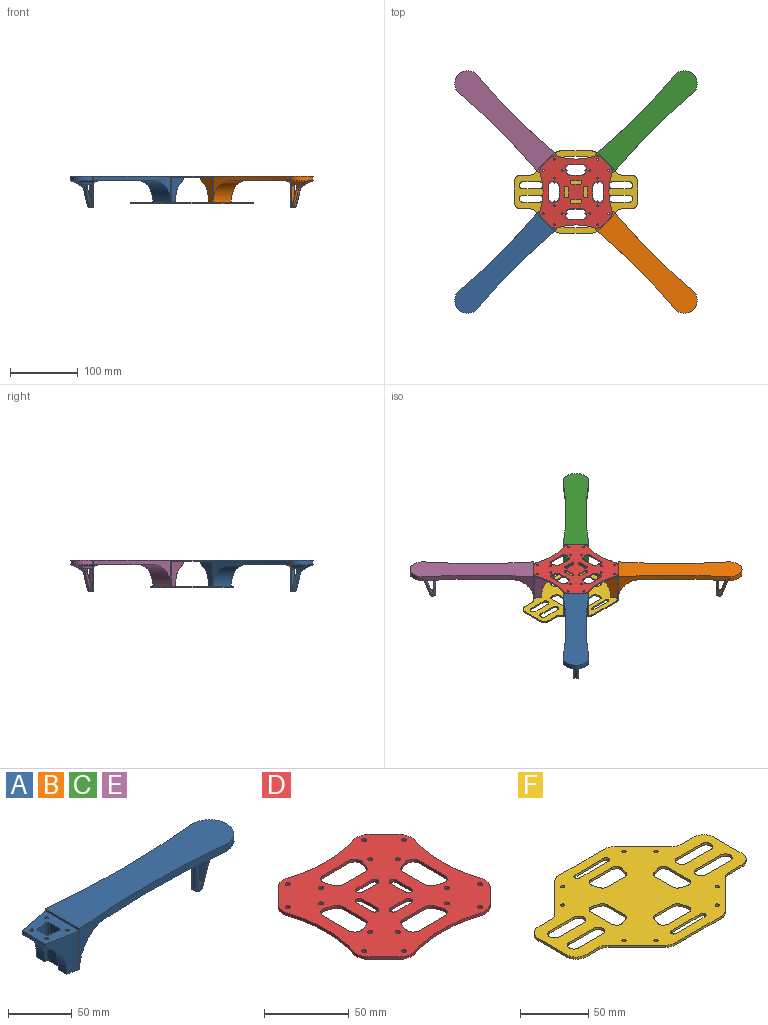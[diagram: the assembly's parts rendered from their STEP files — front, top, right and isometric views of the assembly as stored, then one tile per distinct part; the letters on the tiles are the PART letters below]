
ASSEMBLY  parts=6 mates=5
PART A: 66 faces, bbox 214.6x38.9x48 mm
  f0: plane 0.16x0.01mm, normal (0,-1,0), area 0mm2, adj f5,f44,f63
  f1: plane 0.16x0.01mm, normal (0,1,0), area 0mm2, adj f3,f46,f63
  f2: plane 19.09x12.46mm, normal (0.45,0,-0.89), area 107.7mm2, adj f4,f6,f34,f43,f52,f57
  f3: cylinder r=5mm len=41.67mm, axis (-1,0,0), area 242.4mm2, adj f1,f4,f7,f34,f39,f47,f60
  f4: bspline ~14.02x6.57mm, area 32.6mm2, adj f2,f3,f34,f52
  f5: cylinder r=5mm len=41.67mm, axis (1,0,0), area 242.4mm2, adj f0,f6,f7,f34,f38,f45,f60
  f6: bspline ~17.01x8.06mm, area 32.6mm2, adj f2,f5,f34,f57
  f7: plane 147.98x38.01mm, normal (0,0,-1), area 4011.6mm2, adj f3,f5,f9,f10,f11,f32,f33,f34
  f8: plane 181.92x38.01mm, normal (0,0,1), area 5871.4mm2, adj f10,f11,f31,f32,f33,f34,f35,f36
  f9: cylinder r=31.8mm len=37.96mm, axis (0,1,0), area 1777.7mm2, adj f7,f13,f32,f33,f35,f36
  f10: plane 7x0.96mm, normal (0,-1,0), area 6.7mm2, adj f7,f8,f33,f34
  f11: plane 7x0.96mm, normal (0,1,0), area 6.7mm2, adj f7,f8,f32,f34
  f12: extruded ~33.43x30.75mm, area 739mm2, adj f13,f15,f17,f18,f19,f22,f23,f24
  f13: plane 37.92x12mm, normal (0,0,-1), area 370mm2, adj f9,f12,f15,f17,f20,f21,f23,f27
  f14: plane 37.92x31.65mm, normal (0,0,1), area 800.9mm2, adj f15,f16,f17,f19,f20,f21,f22,f23
  f15: plane 37.07x30.99mm, normal (-0.19,0.98,0), area 651.5mm2, adj f12,f13,f14,f16,f18,f36
  f16: plane 25.93x1.4mm, normal (-1,0,0), area 36.3mm2, adj f14,f15,f17,f18
  f17: plane 37.07x30.99mm, normal (-0.19,-0.98,0), area 651.5mm2, adj f12,f13,f14,f16,f18,f35
  f18: cylinder r=5mm len=27.13mm, axis (0,1,0), area 158.4mm2, adj f12,f15,f16,f17
  f19: cylinder r=1.5mm len=8.24mm, axis (0,0,1), area 69.7mm2, adj f12,f14
  f20: cylinder r=1.5mm len=36.8mm, axis (0,0,1), area 346.8mm2, adj f13,f14
  f21: cylinder r=1.5mm len=36.8mm, axis (0,0,1), area 346.8mm2, adj f13,f14
  f22: cylinder r=1.5mm len=8.24mm, axis (0,0,1), area 69.7mm2, adj f12,f14
  f23: plane 36.8x9.65mm, normal (0.19,-0.98,0), area 183.9mm2, adj f12,f13,f14,f24,f29
  f24: cylinder r=2mm len=10.6mm, axis (0,0,1), area 27.5mm2, adj f12,f14,f23,f25
  f25: plane 9.27x7.73mm, normal (1,0,0), area 71.6mm2, adj f12,f14,f24,f26
  f26: cylinder r=2mm len=10.6mm, axis (0,0,1), area 27.5mm2, adj f12,f14,f25,f27
  f27: plane 36.8x9.65mm, normal (0.19,0.98,0), area 183.9mm2, adj f12,f13,f14,f26,f30
  f28: plane 36.8x11.41mm, normal (-1,0,0), area 419.9mm2, adj f13,f14,f29,f30
  f29: cylinder r=2mm len=36.8mm, axis (0,0,1), area 129.5mm2, adj f13,f14,f23,f28
  f30: cylinder r=2mm len=36.8mm, axis (0,0,1), area 129.5mm2, adj f13,f14,f27,f28
  f31: plane 37.92x2mm, normal (-1,0,0), area 75.8mm2, adj f8,f14,f35,f36
  f32: cylinder r=800mm len=161.71mm, axis (0,0,-1), area 1344.7mm2, adj f7,f8,f9,f11,f36
  f33: cylinder r=800mm len=161.71mm, axis (0,0,-1), area 1344.7mm2, adj f7,f8,f9,f10,f35
  f34: cylinder r=19mm len=38.01mm, axis (0,0,-1), area 424.8mm2, adj f2,f3,f4,f5,f6,f7,f8,f10
  f35: cylinder r=10mm len=38.8mm, axis (0,0,1), area 43.5mm2, adj f8,f9,f13,f14,f17,f31,f33
  f36: cylinder r=10mm len=38.8mm, axis (0,0,-1), area 43.5mm2, adj f8,f9,f13,f14,f15,f31,f32
  f37: plane 24.74x8.67mm, normal (0.94,0,-0.33), area 91.7mm2, adj f41,f43,f50,f55
  f38: plane 32.81x18.54mm, normal (0,-1,0), area 52.4mm2, adj f5,f44,f54,f55,f56,f57,f58,f59
  f39: plane 32.81x18.54mm, normal (0,1,0), area 52.4mm2, adj f3,f46,f49,f50,f51,f52,f58,f59
  f40: cylinder r=5mm len=17.5mm, axis (0,1,0), area 46.6mm2, adj f7,f45,f47
  f41: cylinder r=5mm len=4.2mm, axis (0,1,0), area 19.6mm2, adj f37,f42,f48,f49,f53,f54
  f42: cylinder r=5mm len=4.32mm, axis (0,1,0), area 15.8mm2, adj f41,f44,f46,f48,f53
  f43: cylinder r=5mm len=3.5mm, axis (0,-1,0), area 13.5mm2, adj f2,f37,f51,f56
  f44: cylinder r=5mm len=33mm, axis (0,0,1), area 164.3mm2, adj f0,f38,f42,f45,f46,f53,f63,f64
  f45: bspline ~10x10mm, area 45.7mm2, adj f5,f40,f44,f47
  f46: cylinder r=5mm len=33mm, axis (0,0,-1), area 164.3mm2, adj f1,f39,f42,f44,f47,f48,f63,f64
  f47: bspline ~10x10mm, area 45.7mm2, adj f3,f40,f45,f46
  f48: bspline ~5.97x3.67mm, area 10.7mm2, adj f41,f42,f46,f49
  f49: torus R=3mm, axis (0,-1,0), area 11.8mm2, adj f39,f41,f48,f50
  f50: cylinder r=2mm len=25.4mm, axis (0.33,0,0.94), area 82.4mm2, adj f37,f39,f49,f51
  f51: torus R=7mm, axis (0,-1,0), area 13.9mm2, adj f39,f43,f50,f52
  f52: cylinder r=2mm len=5.5mm, axis (0.89,0,0.45), area 16.2mm2, adj f2,f4,f39,f51
  f53: bspline ~5.97x3.67mm, area 10.7mm2, adj f41,f42,f44,f54
  f54: torus R=3mm, axis (0,-1,0), area 11.8mm2, adj f38,f41,f53,f55
  f55: cylinder r=2mm len=25.4mm, axis (-0.33,0,-0.94), area 82.4mm2, adj f37,f38,f54,f56
  f56: torus R=7mm, axis (0,-1,0), area 13.9mm2, adj f38,f43,f55,f57
  f57: cylinder r=2mm len=5.5mm, axis (-0.89,0,-0.45), area 16.2mm2, adj f2,f6,f38,f56
  f58: plane 23.99x8.4mm, normal (-0.94,0,0.33), area 190.7mm2, adj f38,f39,f59,f62
  f59: cylinder r=2mm len=7.5mm, axis (0,-1,0), area 28.6mm2, adj f38,f39,f58,f60
  f60: plane 8.6x7.5mm, normal (0,0,-1), area 64.5mm2, adj f3,f5,f59,f63
  f61: plane 7.5x0.2mm, normal (0,0,1), area 1.5mm2, adj f38,f39,f62,f64
  f62: cylinder r=2mm len=7.5mm, axis (0,-1,0), area 18.5mm2, adj f38,f39,f58,f61
  f63: cylinder r=2mm len=7.5mm, axis (0,-1,0), area 22.5mm2, adj f0,f1,f44,f46,f60,f65
  f64: cylinder r=2mm len=7.5mm, axis (0,-1,0), area 22.5mm2, adj f38,f39,f44,f46,f61,f65
  f65: plane 23.99x6.8mm, normal (1,0,0), area 163.1mm2, adj f44,f46,f63,f64
PART B: same geometry as A
PART C: same geometry as A
PART D: 82 faces, bbox 106.8x106.8x2 mm
  f0: plane 106.75x106.75mm, normal (0,0,1), area 7803.2mm2, adj f2,f3,f4,f5,f6,f7,f8,f9
  f1: plane 106.75x106.75mm, normal (0,0,-1), area 7803.2mm2, adj f2,f3,f4,f5,f6,f7,f8,f9
  f2: plane 12.51x12.51mm, normal (0.71,0.71,0), area 35.4mm2, adj f0,f1,f10,f12
  f3: plane 12.51x12.51mm, normal (-0.71,0.71,0), area 35.4mm2, adj f0,f1,f13,f16
  f4: plane 12.51x12.51mm, normal (-0.71,-0.71,0), area 35.4mm2, adj f0,f1,f14,f17
  f5: plane 12.51x12.51mm, normal (0.71,-0.71,0), area 35.4mm2, adj f0,f1,f11,f15
  f6: cylinder r=90mm len=55.57mm, axis (0,0,-1), area 113mm2, adj f0,f1,f16,f17
  f7: cylinder r=90mm len=55.57mm, axis (0,0,-1), area 113mm2, adj f0,f1,f14,f15
  f8: cylinder r=90mm len=55.57mm, axis (0,0,-1), area 113mm2, adj f0,f1,f12,f13
  f9: cylinder r=90mm len=55.57mm, axis (0,0,-1), area 113mm2, adj f0,f1,f10,f11
  f10: cylinder r=10mm len=10.16mm, axis (0,0,-1), area 22mm2, adj f0,f1,f2,f9
  f11: cylinder r=10mm len=10.16mm, axis (0,0,-1), area 22mm2, adj f0,f1,f5,f9
  f12: cylinder r=10mm len=10.16mm, axis (0,0,-1), area 22mm2, adj f0,f1,f2,f8
  f13: cylinder r=10mm len=10.16mm, axis (0,0,-1), area 22mm2, adj f0,f1,f3,f8
  f14: cylinder r=10mm len=10.16mm, axis (0,0,-1), area 22mm2, adj f0,f1,f4,f7
  f15: cylinder r=10mm len=10.16mm, axis (0,0,-1), area 22mm2, adj f0,f1,f5,f7
  f16: cylinder r=10mm len=10.16mm, axis (0,0,-1), area 22mm2, adj f0,f1,f3,f6
  f17: cylinder r=10mm len=10.16mm, axis (0,0,-1), area 22mm2, adj f0,f1,f4,f6
  f18: cylinder r=1.5mm len=3mm, axis (0,0,1), area 18.8mm2, adj f0,f1
  f19: cylinder r=1.5mm len=3mm, axis (0,0,1), area 18.8mm2, adj f0,f1
  f20: cylinder r=1.5mm len=3mm, axis (0,0,1), area 18.8mm2, adj f0,f1
  f21: cylinder r=1.5mm len=3mm, axis (0,0,1), area 18.8mm2, adj f0,f1
  f22: cylinder r=1.5mm len=3mm, axis (0,0,1), area 18.8mm2, adj f0,f1
  f23: cylinder r=1.5mm len=3mm, axis (0,0,1), area 18.8mm2, adj f0,f1
  f24: cylinder r=1.5mm len=3mm, axis (0,0,1), area 18.8mm2, adj f0,f1
  f25: cylinder r=1.5mm len=3mm, axis (0,0,1), area 18.8mm2, adj f0,f1
  f26: cylinder r=1.5mm len=3mm, axis (0,0,1), area 18.8mm2, adj f0,f1
  f27: cylinder r=1.5mm len=3mm, axis (0,0,1), area 18.8mm2, adj f0,f1
  f28: cylinder r=1.5mm len=3mm, axis (0,0,1), area 18.8mm2, adj f0,f1
  f29: cylinder r=1.5mm len=3mm, axis (0,0,1), area 18.8mm2, adj f0,f1
  f30: cylinder r=1.5mm len=3mm, axis (0,0,1), area 18.8mm2, adj f0,f1
  f31: cylinder r=1.5mm len=3mm, axis (0,0,1), area 18.8mm2, adj f0,f1
  f32: cylinder r=1.5mm len=3mm, axis (0,0,1), area 18.8mm2, adj f0,f1
  f33: cylinder r=1.5mm len=3mm, axis (0,0,1), area 18.8mm2, adj f0,f1
  f34: plane 12.5x2mm, normal (0,-1,0), area 25mm2, adj f0,f1,f35,f37
  f35: cylinder r=2.5mm len=5mm, axis (0,0,1), area 15.7mm2, adj f0,f1,f34,f36
  f36: plane 12.5x2mm, normal (0,1,0), area 25mm2, adj f0,f1,f35,f37
  f37: cylinder r=2.5mm len=5mm, axis (0,0,1), area 15.7mm2, adj f0,f1,f34,f36
  f38: plane 5x2mm, normal (0.32,0.95,0), area 10.5mm2, adj f0,f1,f39,f45
  f39: cylinder r=5mm len=6.58mm, axis (0,0,1), area 18.9mm2, adj f0,f1,f38,f40
  f40: plane 21.13x2mm, normal (-1,0,0), area 42.3mm2, adj f0,f1,f39,f41
  f41: cylinder r=5mm len=6.58mm, axis (0,0,1), area 18.9mm2, adj f0,f1,f40,f42
  f42: plane 5x2mm, normal (0.32,-0.95,0), area 10.5mm2, adj f0,f1,f41,f43
  f43: cylinder r=5mm len=4.74mm, axis (0,0,1), area 12.5mm2, adj f0,f1,f42,f44
  f44: plane 17.79x2mm, normal (1,0,0), area 35.6mm2, adj f0,f1,f43,f45
  f45: cylinder r=5mm len=4.74mm, axis (0,0,1), area 12.5mm2, adj f0,f1,f38,f44
  f46: cylinder r=5mm len=6.58mm, axis (0,0,1), area 18.9mm2, adj f0,f1,f47,f53
  f47: plane 21.13x2mm, normal (1,0,0), area 42.3mm2, adj f0,f1,f46,f48
  f48: cylinder r=5mm len=6.58mm, axis (0,0,1), area 18.9mm2, adj f0,f1,f47,f49
  f49: plane 5x2mm, normal (-0.32,0.95,0), area 10.5mm2, adj f0,f1,f48,f50
  f50: cylinder r=5mm len=4.74mm, axis (0,0,1), area 12.5mm2, adj f0,f1,f49,f51
  f51: plane 17.79x2mm, normal (-1,0,0), area 35.6mm2, adj f0,f1,f50,f52
  f52: cylinder r=5mm len=4.74mm, axis (0,0,1), area 12.5mm2, adj f0,f1,f51,f53
  f53: plane 5x2mm, normal (-0.32,-0.95,0), area 10.5mm2, adj f0,f1,f46,f52
  f54: plane 17.79x2mm, normal (0,-1,0), area 35.6mm2, adj f0,f1,f55,f61
  f55: cylinder r=5mm len=4.74mm, axis (0,0,1), area 12.5mm2, adj f0,f1,f54,f56
  f56: plane 5x2mm, normal (0.95,-0.32,0), area 10.5mm2, adj f0,f1,f55,f57
  f57: cylinder r=5mm len=6.58mm, axis (0,0,1), area 18.9mm2, adj f0,f1,f56,f58
  f58: plane 21.13x2mm, normal (0,1,0), area 42.3mm2, adj f0,f1,f57,f59
  f59: cylinder r=5mm len=6.58mm, axis (0,0,1), area 18.9mm2, adj f0,f1,f58,f60
  f60: plane 5x2mm, normal (-0.95,-0.32,0), area 10.5mm2, adj f0,f1,f59,f61
  f61: cylinder r=5mm len=4.74mm, axis (0,0,1), area 12.5mm2, adj f0,f1,f54,f60
  f62: cylinder r=2.5mm len=5mm, axis (0,0,1), area 15.7mm2, adj f0,f1,f63,f65
  f63: plane 12.5x2mm, normal (0,1,0), area 25mm2, adj f0,f1,f62,f64
  f64: cylinder r=2.5mm len=5mm, axis (0,0,1), area 15.7mm2, adj f0,f1,f63,f65
  f65: plane 12.5x2mm, normal (0,-1,0), area 25mm2, adj f0,f1,f62,f64
  f66: cylinder r=2.5mm len=5mm, axis (0,0,1), area 15.7mm2, adj f0,f1,f67,f69
  f67: plane 12.5x2mm, normal (1,0,0), area 25mm2, adj f0,f1,f66,f68
  f68: cylinder r=2.5mm len=5mm, axis (0,0,1), area 15.7mm2, adj f0,f1,f67,f69
  f69: plane 12.5x2mm, normal (-1,0,0), area 25mm2, adj f0,f1,f66,f68
  f70: cylinder r=2.5mm len=5mm, axis (0,0,1), area 15.7mm2, adj f0,f1,f71,f73
  f71: plane 12.5x2mm, normal (1,0,0), area 25mm2, adj f0,f1,f70,f72
  f72: cylinder r=2.5mm len=5mm, axis (0,0,1), area 15.7mm2, adj f0,f1,f71,f73
  f73: plane 12.5x2mm, normal (-1,0,0), area 25mm2, adj f0,f1,f70,f72
  f74: plane 21.13x2mm, normal (0,-1,0), area 42.3mm2, adj f0,f1,f75,f81
  f75: cylinder r=5mm len=6.58mm, axis (0,0,1), area 18.9mm2, adj f0,f1,f74,f76
  f76: plane 5x2mm, normal (0.95,0.32,0), area 10.5mm2, adj f0,f1,f75,f77
  f77: cylinder r=5mm len=4.74mm, axis (0,0,1), area 12.5mm2, adj f0,f1,f76,f78
  f78: plane 17.79x2mm, normal (0,1,0), area 35.6mm2, adj f0,f1,f77,f79
  f79: cylinder r=5mm len=4.74mm, axis (0,0,1), area 12.5mm2, adj f0,f1,f78,f80
  f80: plane 5x2mm, normal (-0.95,0.32,0), area 10.5mm2, adj f0,f1,f79,f81
  f81: cylinder r=5mm len=6.58mm, axis (0,0,1), area 18.9mm2, adj f0,f1,f74,f80
PART E: same geometry as A
PART F: 90 faces, bbox 182x121x2 mm
  f0: plane 182x121mm, normal (0,0,1), area 12080mm2, adj f2,f3,f4,f5,f6,f7,f8,f9
  f1: plane 182x121mm, normal (0,0,-1), area 12080mm2, adj f2,f3,f4,f5,f6,f7,f8,f9
  f2: plane 29.75x29.75mm, normal (-0.71,-0.71,0), area 84.2mm2, adj f0,f1,f3,f25
  f3: cylinder r=10mm len=7.07mm, axis (0,0,-1), area 15.7mm2, adj f0,f1,f2,f4
  f4: plane 47.49x2mm, normal (0,-1,0), area 95mm2, adj f0,f1,f3,f5
  f5: cylinder r=10mm len=7.07mm, axis (0,0,-1), area 15.7mm2, adj f0,f1,f4,f6
  f6: plane 29.75x29.75mm, normal (0.71,-0.71,0), area 84.2mm2, adj f0,f1,f5,f7
  f7: cylinder r=10mm len=7.07mm, axis (0,0,-1), area 15.7mm2, adj f0,f1,f6,f8
  f8: plane 13.36x2mm, normal (0,-1,0), area 26.7mm2, adj f0,f1,f7,f9
  f9: cylinder r=10mm len=10mm, axis (0,0,-1), area 31.4mm2, adj f0,f1,f8,f10
  f10: plane 29.78x2mm, normal (1,0,0), area 59.6mm2, adj f0,f1,f9,f11
  f11: cylinder r=10mm len=10mm, axis (0,0,-1), area 31.4mm2, adj f0,f1,f10,f12
  f12: plane 13.36x2mm, normal (0,1,0), area 26.7mm2, adj f0,f1,f11,f13
  f13: cylinder r=10mm len=7.07mm, axis (0,0,-1), area 15.7mm2, adj f0,f1,f12,f14
  f14: plane 29.75x29.75mm, normal (0.71,0.71,0), area 84.2mm2, adj f0,f1,f13,f15
  f15: cylinder r=10mm len=7.07mm, axis (0,0,-1), area 15.7mm2, adj f0,f1,f14,f16
  f16: plane 47.49x2mm, normal (0,1,0), area 95mm2, adj f0,f1,f15,f17
  f17: cylinder r=10mm len=7.07mm, axis (0,0,-1), area 15.7mm2, adj f0,f1,f16,f18
  f18: plane 29.75x29.75mm, normal (-0.71,0.71,0), area 84.2mm2, adj f0,f1,f17,f19
  f19: cylinder r=10mm len=7.07mm, axis (0,0,-1), area 15.7mm2, adj f0,f1,f18,f20
  f20: plane 13.36x2mm, normal (0,1,0), area 26.7mm2, adj f0,f1,f19,f21
  f21: cylinder r=10mm len=10mm, axis (0,0,-1), area 31.4mm2, adj f0,f1,f20,f22
  f22: plane 29.78x2mm, normal (-1,0,0), area 59.6mm2, adj f0,f1,f21,f23
  f23: cylinder r=10mm len=10mm, axis (0,0,-1), area 31.4mm2, adj f0,f1,f22,f24
  f24: plane 13.36x2mm, normal (0,-1,0), area 26.7mm2, adj f0,f1,f23,f25
  f25: cylinder r=10mm len=7.07mm, axis (0,0,-1), area 15.7mm2, adj f0,f1,f2,f24
  f26: cylinder r=1.5mm len=3mm, axis (0,0,1), area 18.8mm2, adj f0,f1
  f27: cylinder r=1.5mm len=3mm, axis (0,0,1), area 18.8mm2, adj f0,f1
  f28: cylinder r=1.5mm len=3mm, axis (0,0,1), area 18.8mm2, adj f0,f1
  f29: cylinder r=1.5mm len=3mm, axis (0,0,1), area 18.8mm2, adj f0,f1
  f30: cylinder r=1.5mm len=3mm, axis (0,0,1), area 18.8mm2, adj f0,f1
  f31: cylinder r=1.5mm len=3mm, axis (0,0,1), area 18.8mm2, adj f0,f1
  f32: cylinder r=1.5mm len=3mm, axis (0,0,1), area 18.8mm2, adj f0,f1
  f33: cylinder r=1.5mm len=3mm, axis (0,0,1), area 18.8mm2, adj f0,f1
  f34: plane 21.13x2mm, normal (0,-1,0), area 42.3mm2, adj f0,f1,f35,f41
  f35: cylinder r=5mm len=6.58mm, axis (0,0,1), area 18.9mm2, adj f0,f1,f34,f36
  f36: plane 5x2mm, normal (0.95,0.32,0), area 10.5mm2, adj f0,f1,f35,f37
  f37: cylinder r=5mm len=4.74mm, axis (0,0,1), area 12.5mm2, adj f0,f1,f36,f38
  f38: plane 17.79x2mm, normal (0,1,0), area 35.6mm2, adj f0,f1,f37,f39
  f39: cylinder r=5mm len=4.74mm, axis (0,0,1), area 12.5mm2, adj f0,f1,f38,f40
  f40: plane 5x2mm, normal (-0.95,0.32,0), area 10.5mm2, adj f0,f1,f39,f41
  f41: cylinder r=5mm len=6.58mm, axis (0,0,1), area 18.9mm2, adj f0,f1,f34,f40
  f42: cylinder r=5mm len=10mm, axis (0,0,1), area 31.4mm2, adj f0,f1,f43,f45
  f43: plane 25x2mm, normal (0,-1,0), area 50mm2, adj f0,f1,f42,f44
  f44: cylinder r=5mm len=10mm, axis (0,0,1), area 31.4mm2, adj f0,f1,f43,f45
  f45: plane 25x2mm, normal (0,1,0), area 50mm2, adj f0,f1,f42,f44
  f46: cylinder r=5mm len=10mm, axis (0,0,1), area 31.4mm2, adj f0,f1,f47,f49
  f47: plane 25x2mm, normal (0,1,0), area 50mm2, adj f0,f1,f46,f48
  f48: cylinder r=5mm len=10mm, axis (0,0,1), area 31.4mm2, adj f0,f1,f47,f49
  f49: plane 25x2mm, normal (0,-1,0), area 50mm2, adj f0,f1,f46,f48
  f50: cylinder r=5mm len=10mm, axis (0,0,1), area 31.4mm2, adj f0,f1,f51,f53
  f51: plane 25x2mm, normal (0,-1,0), area 50mm2, adj f0,f1,f50,f52
  f52: cylinder r=5mm len=10mm, axis (0,0,1), area 31.4mm2, adj f0,f1,f51,f53
  f53: plane 25x2mm, normal (0,1,0), area 50mm2, adj f0,f1,f50,f52
  f54: plane 30x2mm, normal (0,-1,0), area 60mm2, adj f0,f1,f55,f57
  f55: cylinder r=2.5mm len=5mm, axis (0,0,1), area 15.7mm2, adj f0,f1,f54,f56
  f56: plane 30x2mm, normal (0,1,0), area 60mm2, adj f0,f1,f55,f57
  f57: cylinder r=2.5mm len=5mm, axis (0,0,1), area 15.7mm2, adj f0,f1,f54,f56
  f58: plane 17.79x2mm, normal (0,-1,0), area 35.6mm2, adj f0,f1,f59,f65
  f59: cylinder r=5mm len=4.74mm, axis (0,0,1), area 12.5mm2, adj f0,f1,f58,f60
  f60: plane 5x2mm, normal (0.95,-0.32,0), area 10.5mm2, adj f0,f1,f59,f61
  f61: cylinder r=5mm len=6.58mm, axis (0,0,1), area 18.9mm2, adj f0,f1,f60,f62
  f62: plane 21.13x2mm, normal (0,1,0), area 42.3mm2, adj f0,f1,f61,f63
  f63: cylinder r=5mm len=6.58mm, axis (0,0,1), area 18.9mm2, adj f0,f1,f62,f64
  f64: plane 5x2mm, normal (-0.95,-0.32,0), area 10.5mm2, adj f0,f1,f63,f65
  f65: cylinder r=5mm len=4.74mm, axis (0,0,1), area 12.5mm2, adj f0,f1,f58,f64
  f66: cylinder r=5mm len=6.58mm, axis (0,0,1), area 18.9mm2, adj f0,f1,f67,f73
  f67: plane 21.13x2mm, normal (1,0,0), area 42.3mm2, adj f0,f1,f66,f68
  f68: cylinder r=5mm len=6.58mm, axis (0,0,1), area 18.9mm2, adj f0,f1,f67,f69
  f69: plane 5x2mm, normal (-0.32,0.95,0), area 10.5mm2, adj f0,f1,f68,f70
  f70: cylinder r=5mm len=4.74mm, axis (0,0,1), area 12.5mm2, adj f0,f1,f69,f71
  f71: plane 17.79x2mm, normal (-1,0,0), area 35.6mm2, adj f0,f1,f70,f72
  f72: cylinder r=5mm len=4.74mm, axis (0,0,1), area 12.5mm2, adj f0,f1,f71,f73
  f73: plane 5x2mm, normal (-0.32,-0.95,0), area 10.5mm2, adj f0,f1,f66,f72
  f74: plane 5x2mm, normal (0.32,0.95,0), area 10.5mm2, adj f0,f1,f75,f81
  f75: cylinder r=5mm len=6.58mm, axis (0,0,1), area 18.9mm2, adj f0,f1,f74,f76
  f76: plane 21.13x2mm, normal (-1,0,0), area 42.3mm2, adj f0,f1,f75,f77
  f77: cylinder r=5mm len=6.58mm, axis (0,0,1), area 18.9mm2, adj f0,f1,f76,f78
  f78: plane 5x2mm, normal (0.32,-0.95,0), area 10.5mm2, adj f0,f1,f77,f79
  f79: cylinder r=5mm len=4.74mm, axis (0,0,1), area 12.5mm2, adj f0,f1,f78,f80
  f80: plane 17.79x2mm, normal (1,0,0), area 35.6mm2, adj f0,f1,f79,f81
  f81: cylinder r=5mm len=4.74mm, axis (0,0,1), area 12.5mm2, adj f0,f1,f74,f80
  f82: plane 25x2mm, normal (0,-1,0), area 50mm2, adj f0,f1,f83,f85
  f83: cylinder r=5mm len=10mm, axis (0,0,1), area 31.4mm2, adj f0,f1,f82,f84
  f84: plane 25x2mm, normal (0,1,0), area 50mm2, adj f0,f1,f83,f85
  f85: cylinder r=5mm len=10mm, axis (0,0,1), area 31.4mm2, adj f0,f1,f82,f84
  f86: cylinder r=2.5mm len=5mm, axis (0,0,1), area 15.7mm2, adj f0,f1,f87,f89
  f87: plane 30x2mm, normal (0,-1,0), area 60mm2, adj f0,f1,f86,f88
  f88: cylinder r=2.5mm len=5mm, axis (0,0,1), area 15.7mm2, adj f0,f1,f87,f89
  f89: plane 30x2mm, normal (0,1,0), area 60mm2, adj f0,f1,f86,f88
PLACE A rot(axis=(0,0,-1),135deg) t=(-33.15,-33.15,-1)mm
PLACE B rot(axis=(0,0,-1),45deg) t=(33.15,-33.15,-1)mm
PLACE C rot(axis=(0,0,1),45deg) t=(33.15,33.15,-1)mm
PLACE D at identity fixed
PLACE E rot(axis=(0,0,1),135deg) t=(-33.15,33.15,-1)mm
PLACE F t=(0,0,-38.8)mm
MATE revolute C.f21 <-> D.f28  axis (0,0,1) through (48.4,31.78,-1)mm
MATE fastened F.f27 <-> D.f29  axis (0,0,1) through (31.78,48.4,-37.8)mm
MATE revolute A.f20 <-> D.f22  axis (0,0,1) through (-31.78,-48.4,-1)mm
MATE revolute E.f20 <-> D.f33  axis (0,0,1) through (-48.4,31.78,-1)mm
MATE revolute B.f20 <-> D.f26  axis (0,0,1) through (48.4,-31.78,-1)mm
